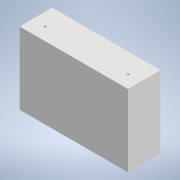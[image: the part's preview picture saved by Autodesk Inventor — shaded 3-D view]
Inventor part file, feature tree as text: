
AUTODESK INVENTOR PART (.ipt)
format: ipt  version: 2022 (Build 260153000, 153)  size: 152,064 bytes
history: native  units: mm
features: sketch x7, extrude x5
ambient origin geometry x8: Origin, YZ Plane, XZ Plane, XY Plane, X Axis, Y Axis, Z Axis, Center Point
bodies: Solid1 (feature_tree)
feature tree (12):
  extrude  "Extrusion1"  Depth=300.0mm
  extrude  "Extrusion2"  Depth=180.0mm
  extrude  "Extrusion4"  Depth=10.0mm
  extrude  "Extrusion5"  Depth=80.0mm TaperAngle=0.0deg
  sketch  "Sketch6"  dims[d18=2.903mm d19=2.903mm]
  sketch  "Sketch7"  dims[d20=2.903mm]
  extrude  "Extrusion6"  Depth=2.903mm
  sketch  "Sketch1"  dims[d0=200.0mm d1=300.0mm]
  sketch  "Sketch2"  dims[d2=90.0mm d3=0.0mm d4=180.0mm]
  sketch  "Sketch4"  dims[d5=280.0mm d6=10.0mm]
  sketch  "Sketch5"  dims[d7=10.0mm d8=80.0mm d9=0.0mm]
  sketch  "Sketch8"  dims[d21=2.903mm d22=5.0mm d23=5.0mm d24=5.0mm d25=5.0mm d26=5.0mm d27=5.0mm d28=5.0mm d29=5.0mm d30=17.0mm d31=0.0mm d32=8.0mm d33=8.0mm d34=35.0mm d35=35.0mm d36=35.0mm d37=35.0mm d38=0.0mm d39=0.0mm d57=5.0mm d58=100.0mm d59=45.0mm d60=10.0mm d61=0.0mm]
